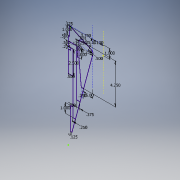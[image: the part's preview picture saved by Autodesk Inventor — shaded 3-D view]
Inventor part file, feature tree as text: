
AUTODESK INVENTOR PART (.ipt)
format: ipt  version: 2017 SP1 (Build 210196100, 196)  size: 128,000 bytes
history: native  units: in
note: dims shown in document units (in); Inventor stores cm internally (conversion verified against a paired STEP export)
features: sketch x1
ambient origin geometry x8: Origin, YZ Plane, XZ Plane, XY Plane, X Axis, Y Axis, Z Axis, Center Point
feature tree (1):
  sketch  "Sketch1"  dims[d0=1.13in d1=3.75in d2=0.125in d3=0.1718in d5=1.0in d6=1.0in d7=90.0deg d8=0.5in d9=15.0deg d12=1.25in d13=0.25in d16=0.5in d17=0.5in d18=0.5in d19=2.5in d20=0.5in d22=0.375in d23=0.25in d25=0.234in d27=0.125in d28=0.25in d29=1.0in d30=4.25in d31=0.25in d33=0.8014in d34=15.0deg d35=0.125in d36=1.0in]
